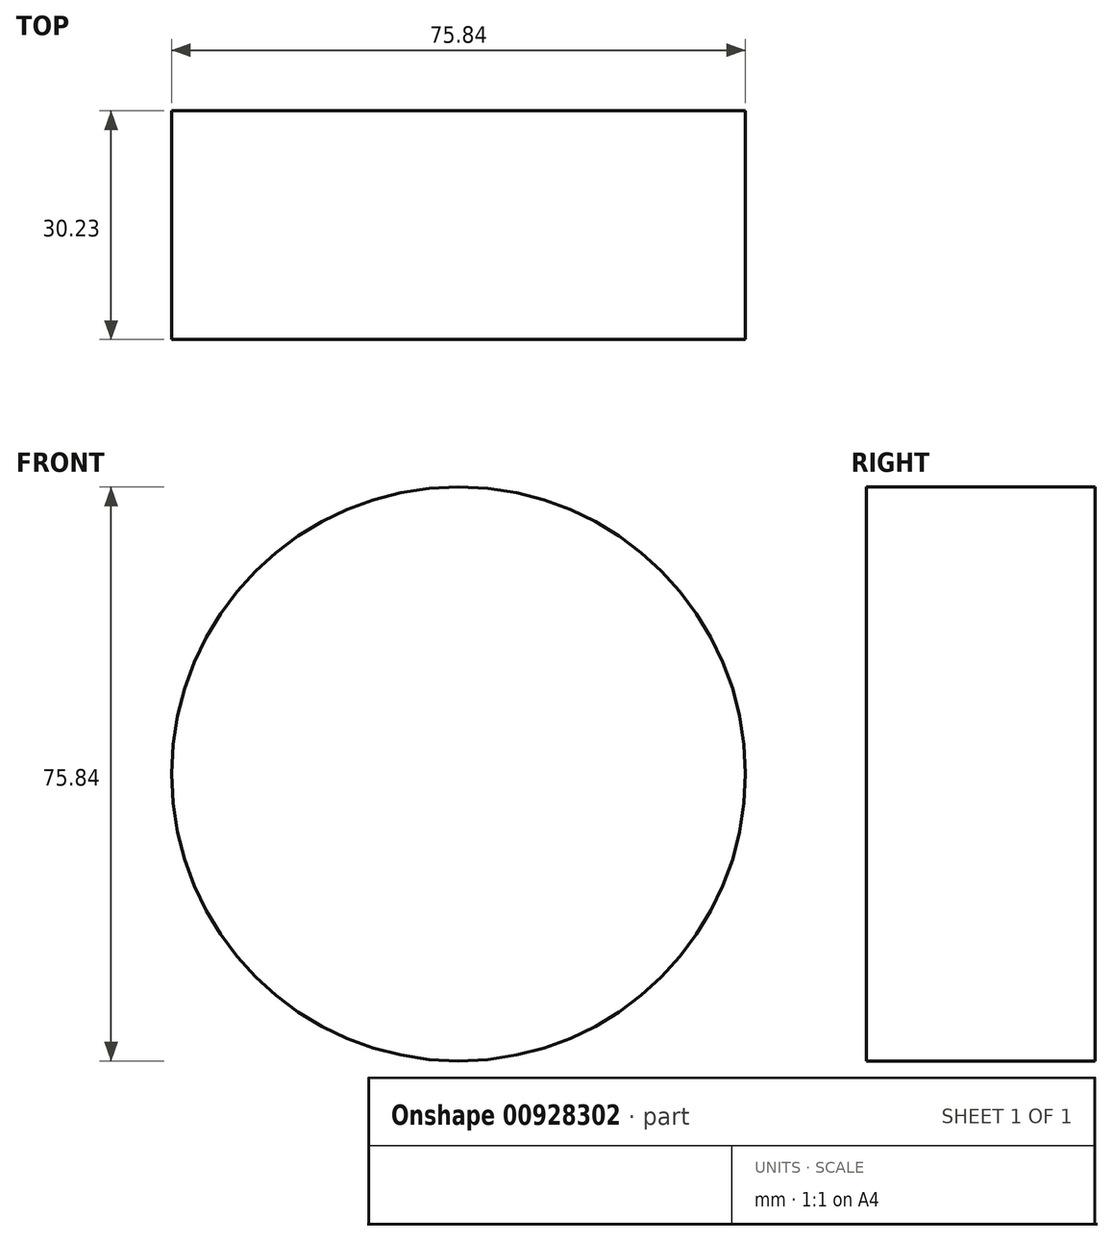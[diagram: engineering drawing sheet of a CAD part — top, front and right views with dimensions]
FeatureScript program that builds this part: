
annotation { "Feature Type Name" : "Feature", "Feature Type Description" : "" }
export const myFeature = defineFeature(function(context is Context, id is Id, definition is map)
    precondition{}
    {
        {
            var Q0;
            Q0=qCreatedBy(makeId("Front.planeOp"),FACE);
            var sketch = newSketch(context, id + "F0", { "sketchPlane" : qUnion([Q0])});
            skCircle(sketch, "E0", {"center": v(0, 0) * mm, "radius": 37.92 * mm});
            skSolve(sketch);
        }
        {
            var Q0;
            Q0 = qSketchRegion(id + "F0", true);
            extrude(context, id + "F1", {"entities" : qUnion([Q0]), "depth" : 30.23 * mm, "offsetDistance" : 25.4 * mm});
        }
    });
